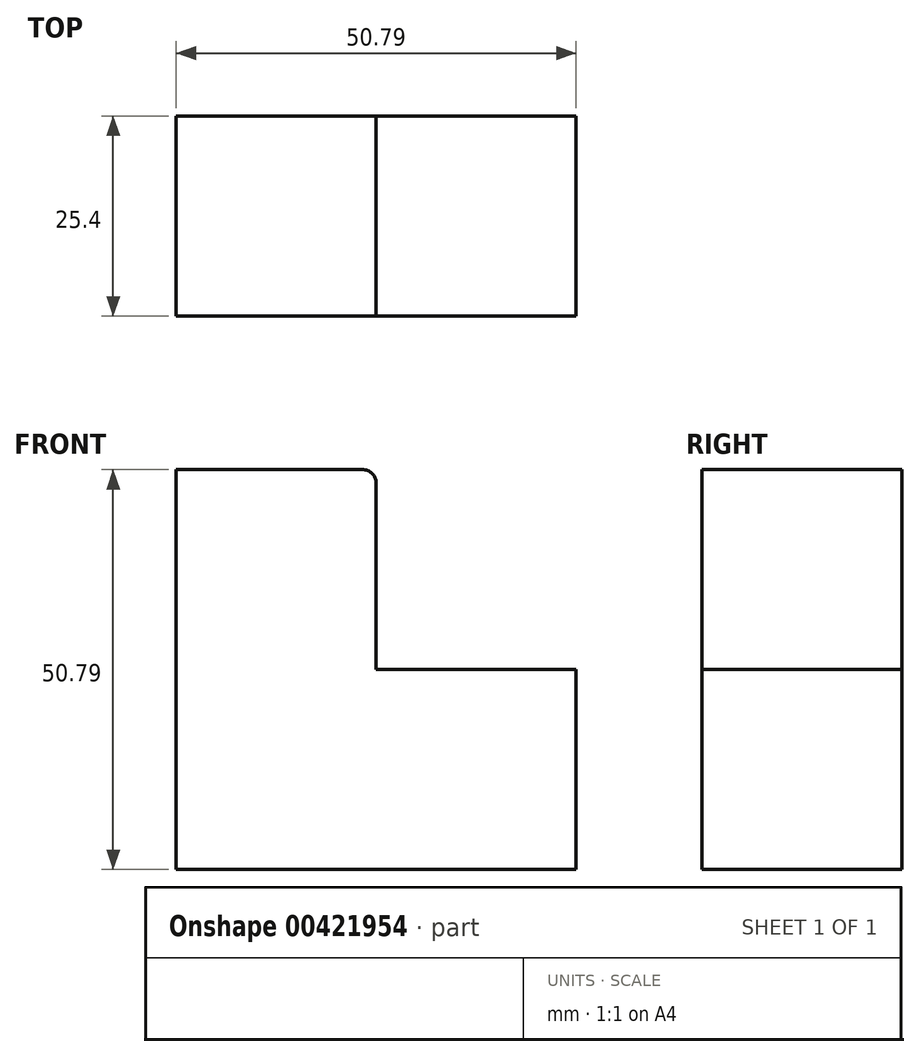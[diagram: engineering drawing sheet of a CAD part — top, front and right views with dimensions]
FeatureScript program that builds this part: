
annotation { "Feature Type Name" : "Feature", "Feature Type Description" : "" }
export const myFeature = defineFeature(function(context is Context, id is Id, definition is map)
    precondition{}
    {
        {
            var Q0;
            Q0=qCreatedBy(makeId("Front.planeOp"),FACE);
            var sketch = newSketch(context, id + "F0", { "sketchPlane" : qUnion([Q0])});
            skLineSegment(sketch, "E0", {"start": v(0, 0) * mm, "end": v(-50.8, 0) * mm});
            skLineSegment(sketch, "E1", {"start": v(-50.8, 0) * mm, "end": v(-50.8, 50.8) * mm});
            skLineSegment(sketch, "E2", {"start": v(-50.8, 50.8) * mm, "end": v(-27.15, 50.8) * mm});
            skLineSegment(sketch, "E3", {"start": v(-25.4, 49.04) * mm, "end": v(-25.4, 25.4) * mm});
            skLineSegment(sketch, "E4", {"start": v(-25.4, 25.4) * mm, "end": v(0, 25.4) * mm});
            skLineSegment(sketch, "E5", {"start": v(0, 25.4) * mm, "end": v(0, -1.9) * mm});
            skPoint(sketch, "E6.visualSharp", {"position": v(-25.4, 50.8) * mm});
            skArc(sketch, "E6.filletArc", {"start": v(-25.4, 49.04) * mm, "mid": v(-25.9, 50.28) * mm, "end": v(-27.15, 50.8) * mm});
            skLineSegment(sketch, "E7", {"start": v(-47.8, 18.9) * mm, "end": v(-25.4, 31.32) * mm});
            skLineSegment(sketch, "E8", {"start": v(-25.4, 31.32) * mm, "end": v(-23.76, 31.32) * mm});
            skLineSegment(sketch, "E9", {"start": v(-33.49, 43.92) * mm, "end": v(74.26, 74.66) * mm});
            skLineSegment(sketch, "E10", {"start": v(-71.3, 70.65) * mm, "end": v(-46.99, 22.91) * mm});
            skSolve(sketch);
        }
        {
            var Q0;
            Q0 = qSketchRegion(id + "F0", true);
            extrude(context, id + "F1", {"entities" : qUnion([Q0]), "depth" : 25.4 * mm});
        }
    });
